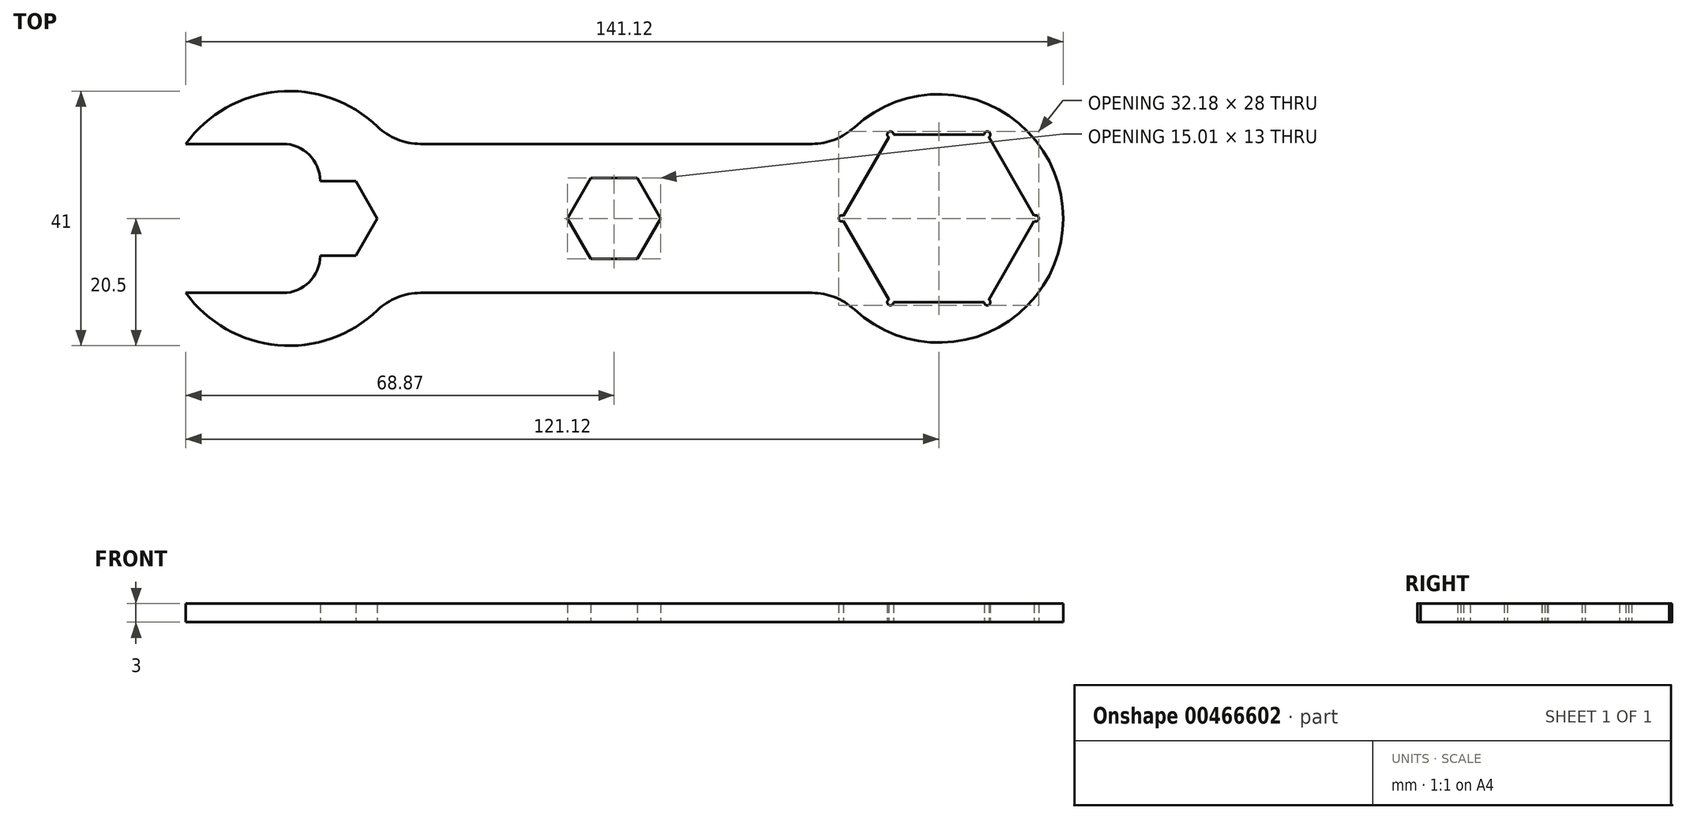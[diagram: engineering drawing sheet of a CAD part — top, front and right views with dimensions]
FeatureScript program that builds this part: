
annotation { "Feature Type Name" : "Feature", "Feature Type Description" : "" }
export const myFeature = defineFeature(function(context is Context, id is Id, definition is map)
    precondition{}
    {
        {
            var Q0;
            Q0=qCreatedBy(makeId("Top.planeOp"),FACE);
            var sketch = newSketch(context, id + "F0", { "sketchPlane" : qUnion([Q0])});
            skCircle(sketch, "E0.cCircle", {"center": v(0, 0) * mm, "radius": 6.5 * mm, "construction": true});
            skLineSegment(sketch, "E0.0", {"start": v(-3.75, 6.5) * mm, "end": v(3.75, 6.5) * mm});
            skLineSegment(sketch, "E0.1", {"start": v(3.75, 6.5) * mm, "end": v(7.5, 0) * mm});
            skLineSegment(sketch, "E0.2", {"start": v(7.5, 0) * mm, "end": v(3.75, -6.5) * mm});
            skLineSegment(sketch, "E0.3", {"start": v(3.75, -6.5) * mm, "end": v(-3.75, -6.5) * mm});
            skLineSegment(sketch, "E0.4", {"start": v(-3.75, -6.5) * mm, "end": v(-7.5, 0) * mm});
            skLineSegment(sketch, "E0.5", {"start": v(-7.5, 0) * mm, "end": v(-3.75, 6.5) * mm});
            skPoint(sketch, "E0.0.midPoint", {"position": v(0, 6.5) * mm});
            skArc(sketch, "E1", {"start": v(38.65, -14.67) * mm, "mid": v(72.25, 0) * mm, "end": v(38.65, 14.67) * mm});
            skArc(sketch, "E2", {"start": v(-38.05, 14.79) * mm, "mid": v(-54.1, 20.42) * mm, "end": v(-68.87, 12) * mm});
            skLineSegment(sketch, "E3.bottom", {"start": v(-31.13, 12) * mm, "end": v(31.85, 12) * mm});
            skLineSegment(sketch, "E3.top", {"start": v(-31.13, -12) * mm, "end": v(31.85, -12) * mm});
            skPoint(sketch, "E3.left.start.orphan", {"position": v(-37.15, 12) * mm});
            skPoint(sketch, "E4.orphan", {"position": v(-37.15, -12) * mm});
            skPoint(sketch, "E5.visualSharp", {"position": v(-35.63, 12) * mm});
            skArc(sketch, "E5.filletArc", {"start": v(-38.05, 14.79) * mm, "mid": v(-34.86, 12.72) * mm, "end": v(-31.13, 12) * mm});
            skPoint(sketch, "E6.visualSharp", {"position": v(-35.63, -12) * mm});
            skArc(sketch, "E6.filletArc", {"start": v(-31.13, -12) * mm, "mid": v(-34.86, -12.72) * mm, "end": v(-38.05, -14.79) * mm});
            skPoint(sketch, "E7.orphan", {"position": v(37.15, 12) * mm});
            skPoint(sketch, "E8.orphan", {"position": v(37.15, -12) * mm});
            skPoint(sketch, "E9.visualSharp", {"position": v(36.25, 12) * mm});
            skArc(sketch, "E9.filletArc", {"start": v(31.85, 12) * mm, "mid": v(35.5, 12.7) * mm, "end": v(38.65, 14.67) * mm});
            skPoint(sketch, "E10.visualSharp", {"position": v(36.25, -12) * mm});
            skArc(sketch, "E10.filletArc", {"start": v(38.65, -14.67) * mm, "mid": v(35.5, -12.7) * mm, "end": v(31.85, -12) * mm});
            skLineSegment(sketch, "E11.bottom", {"start": v(-53.27, 12) * mm, "end": v(-68.87, 12) * mm});
            skLineSegment(sketch, "E11.top", {"start": v(-53.27, -12) * mm, "end": v(-68.87, -12) * mm});
            skLineSegment(sketch, "E11.left", {"start": v(-47.27, 6) * mm, "end": v(-47.27, -6) * mm});
            skPoint(sketch, "E11.middle", {"position": v(-72.75, 0) * mm});
            skArc(sketch, "E12.trimOffspring", {"start": v(-68.87, -12) * mm, "mid": v(-54.1, -20.42) * mm, "end": v(-38.05, -14.79) * mm});
            skPoint(sketch, "E11.right.end.orphan", {"position": v(-98.23, -12) * mm});
            skPoint(sketch, "E11.right.start.orphan", {"position": v(-98.23, 12) * mm});
            skPoint(sketch, "E13.visualSharp", {"position": v(-47.27, 12) * mm});
            skArc(sketch, "E13.filletArc", {"start": v(-47.27, 6) * mm, "mid": v(-49.03, 10.24) * mm, "end": v(-53.27, 12) * mm});
            skPoint(sketch, "E14.visualSharp", {"position": v(-47.27, -12) * mm});
            skArc(sketch, "E14.filletArc", {"start": v(-53.27, -12) * mm, "mid": v(-49.03, -10.24) * mm, "end": v(-47.27, -6) * mm});
            skCircle(sketch, "E15.cCircle", {"center": v(52.25, 0) * mm, "radius": 13.5 * mm, "construction": true});
            skLineSegment(sketch, "E15.0", {"start": v(44.46, 13.5) * mm, "end": v(60.04, 13.5) * mm});
            skLineSegment(sketch, "E15.1", {"start": v(60.04, 13.5) * mm, "end": v(67.84, 0) * mm});
            skLineSegment(sketch, "E15.2", {"start": v(67.84, 0) * mm, "end": v(60.04, -13.5) * mm});
            skLineSegment(sketch, "E15.3", {"start": v(60.04, -13.5) * mm, "end": v(44.46, -13.5) * mm});
            skLineSegment(sketch, "E15.4", {"start": v(44.46, -13.5) * mm, "end": v(36.66, 0) * mm});
            skLineSegment(sketch, "E15.5", {"start": v(36.66, 0) * mm, "end": v(44.46, 13.5) * mm});
            skPoint(sketch, "E15.0.midPoint", {"position": v(52.25, 13.5) * mm});
            skCircle(sketch, "E16", {"center": v(44.46, 13.5) * mm, "radius": 0.5 * mm});
            skCircle(sketch, "E17", {"center": v(60.04, 13.5) * mm, "radius": 0.5 * mm});
            skCircle(sketch, "E18", {"center": v(36.66, 0) * mm, "radius": 0.5 * mm});
            skCircle(sketch, "E19", {"center": v(67.84, 0) * mm, "radius": 0.5 * mm});
            skCircle(sketch, "E20", {"center": v(44.46, -13.5) * mm, "radius": 0.5 * mm});
            skCircle(sketch, "E21", {"center": v(60.04, -13.5) * mm, "radius": 0.5 * mm});
            skCircle(sketch, "E22.cCircle", {"center": v(-45, 0) * mm, "radius": 6 * mm, "construction": true});
            skLineSegment(sketch, "E22.0", {"start": v(-48.46, 6) * mm, "end": v(-41.54, 6) * mm});
            skLineSegment(sketch, "E22.1", {"start": v(-41.54, 6) * mm, "end": v(-38.07, 0) * mm});
            skLineSegment(sketch, "E22.2", {"start": v(-38.07, 0) * mm, "end": v(-41.54, -6) * mm});
            skLineSegment(sketch, "E22.3", {"start": v(-41.54, -6) * mm, "end": v(-48.46, -6) * mm});
            skLineSegment(sketch, "E22.4", {"start": v(-48.46, -6) * mm, "end": v(-51.93, 0) * mm});
            skLineSegment(sketch, "E22.5", {"start": v(-51.93, 0) * mm, "end": v(-48.46, 6) * mm});
            skPoint(sketch, "E22.0.midPoint", {"position": v(-45, 6) * mm});
            skSolve(sketch);
        }
        {
            var Q0;
            Q0=makeQuery(id+"F0.imprint","IMPRINT",FACE,{"disambiguationData":[TD([[makeQuery(id+"F0.imprint","IMPRINT",EDGE,{"derivedFrom":sQuery(id+"F0.wireOp",EDGE,"E1")}),1.0]])]});
            extrude(context, id + "F1", {"entities" : qUnion([Q0]), "depth" : 3 * mm, "offsetDistance" : 25 * mm});
        }
    });
